# Revit family: 756-102-IS5-DN700-800
name_source: partatom
category: Pipe Accessories
units: mm (PartAtom-declared; Revit-internal decimal feet)

## family parameters
Always vertical = Yes
Cut with Voids When Loaded = No
Part Type = Valve - Breaks Into
Round Connector Dimension = Use Diameter
Shared = No
Work Plane-Based = No

## types (4) — shared parameters
A = 313 mm
A2 = 184 mm
Body_wallthickness = 10 mm  [stored 0.0328084 ft]
C_Rod = 38 mm  [stored 0.124672 ft]
D1 = 10 mm  [stored 0.0328084 ft]
DN0700_PN10 = 756-0700-1-04102
DN0700_PN16 = 756-0700-1-14102
DN0800_PN10 = 756-0800-1-04102
DN0800_PN16 = 756-0800-1-14102
Description_ = AVK DOUBLE ECC. BUTTERFLY VALVE, LONG
Disc_width = 40 mm  [stored 0.131234 ft]
Flange_Thickness = 40 mm  [stored 0.131234 ft]
GB_Flange = 5 mm  [stored 0.0164042 ft]
Gear_box_depth = 278 mm
Offset = 3 mm  [stored 0.00984252 ft]
Pin_dia = 60 mm  [stored 0.19685 ft]
RF_Cut_Thickness = 5 mm  [stored 0.0164042 ft]
Rib_depth = 30 mm  [stored 0.0984252 ft]
Search_table = 756-102-IS5-DN700-800
URL_product_pages = https://www.avkvalves.com

## per-type parameters (varying)
- DN0700_PN10: B=605 mm; Bottom_Depth=1050 mm; Bottom_width=395 mm; C=287 mm; DN=700 mm; Disc_Dia=690 mm; Flange_OD=448 mm; GB_Dia=40 mm  [stored 0.131234 ft]; GB_HW=125 mm  [stored 0.410105 ft]; GB_HW_2=42 mm; GB_Ref=17 mm; GB_Width=72 mm  [stored 0.23622 ft]; GB_Width_2=117 mm  [stored 0.383858 ft]; GB_Width_3=130 mm  [stored 0.426509 ft]; GB_Width_Ref=100 mm  [stored 0.328084 ft]; Gear_box_Mount_Flange_width=102 mm; Gear_box_Mount_width=16 mm; H1=565 mm; H2=550 mm; ID (Radius)=350 mm; L=430 mm; L1=127 mm; L2=133 mm  [stored 0.436352 ft]; Pin_Depth=798 mm; Pin_width=215 mm; Rf_Dia=397 mm; Rib_height=407 mm; Rib_height_2=118 mm; Rib_width=350 mm; Rib_width_2=204 mm  [stored 0.669291 ft]; T(Addon)=605 mm; W1=448 mm; W2=656 mm; W2_Ref=125 mm  [stored 0.410105 ft]; W3=533 mm; W4=543 mm
- DN0700_PN16: B=600 mm; Bottom_Depth=1050 mm; Bottom_width=427 mm; C=329 mm; DN=700 mm; Disc_Dia=690 mm; Flange_OD=455 mm; GB_Dia=40 mm  [stored 0.131234 ft]; GB_HW=125 mm  [stored 0.410105 ft]; GB_HW_2=42 mm; GB_Ref=17 mm; GB_Width=114 mm  [stored 0.374016 ft]; GB_Width_2=117 mm  [stored 0.383858 ft]; GB_Width_3=130 mm  [stored 0.426509 ft]; GB_Width_Ref=143 mm  [stored 0.46916 ft]; Gear_box_Mount_Flange_width=107 mm  [stored 0.35105 ft]; Gear_box_Mount_width=17 mm; H1=560 mm; H2=550 mm; ID (Radius)=350 mm; L=430 mm; L1=127 mm; L2=133 mm  [stored 0.436352 ft]; Pin_Depth=805 mm; Pin_width=215 mm; Rf_Dia=397 mm; Rib_height=414 mm; Rib_height_2=105 mm  [stored 0.344488 ft]; Rib_width=350 mm; Rib_width_2=214 mm  [stored 0.7021 ft]; T(Addon)=600 mm; W1=455 mm; W2=656 mm; W2_Ref=110 mm  [stored 0.360892 ft]; W3=533 mm; W4=543 mm
- DN0800_PN10: B=670 mm; Bottom_Depth=1200 mm; Bottom_width=460 mm; C=349 mm; DN=800 mm; Disc_Dia=789 mm; Flange_OD=508 mm; GB_Dia=41 mm; GB_HW=155 mm  [stored 0.50853 ft]; GB_HW_2=52 mm; GB_Ref=21 mm; GB_Width=114 mm  [stored 0.374016 ft]; GB_Width_2=126 mm  [stored 0.413386 ft]; GB_Width_3=140 mm  [stored 0.459318 ft]; GB_Width_Ref=157 mm  [stored 0.515092 ft]; Gear_box_Mount_Flange_width=112 mm; Gear_box_Mount_width=17 mm; H1=630 mm; H2=620 mm; ID (Radius)=400 mm; L=470 mm; L1=156 mm  [stored 0.511811 ft]; L2=162 mm  [stored 0.531496 ft]; Pin_Depth=908 mm; Pin_width=235 mm; Rf_Dia=450 mm; Rib_height=461 mm; Rib_height_2=123 mm; Rib_width=390 mm; Rib_width_2=223 mm; T(Addon)=670 mm; W1=508 mm; W2=735 mm; W2_Ref=155 mm  [stored 0.50853 ft]; W3=627 mm; W4=636 mm
- DN0800_PN16: B=670 mm; Bottom_Depth=1200 mm; Bottom_width=492 mm; C=349 mm; DN=800 mm; Disc_Dia=789 mm; Flange_OD=513 mm; GB_Dia=41 mm; GB_HW=155 mm  [stored 0.50853 ft]; GB_HW_2=52 mm; GB_Ref=21 mm; GB_Width=114 mm  [stored 0.374016 ft]; GB_Width_2=126 mm  [stored 0.413386 ft]; GB_Width_3=140 mm  [stored 0.459318 ft]; GB_Width_Ref=157 mm  [stored 0.515092 ft]; Gear_box_Mount_Flange_width=116 mm  [stored 0.380577 ft]; Gear_box_Mount_width=18 mm  [stored 0.0590551 ft]; H1=630 mm; H2=620 mm; ID (Radius)=400 mm; L=470 mm; L1=156 mm  [stored 0.511811 ft]; L2=162 mm  [stored 0.531496 ft]; Pin_Depth=913 mm; Pin_width=235 mm; Rf_Dia=450 mm; Rib_height=466 mm; Rib_height_2=118 mm; Rib_width=390 mm; Rib_width_2=232 mm; T(Addon)=670 mm; W1=513 mm; W2=735 mm; W2_Ref=155 mm  [stored 0.50853 ft]; W3=627 mm; W4=636 mm

note: [stored X ft] marks values corroborated as IEEE doubles in the binary element streams (Revit-internal decimal feet)

## geometry (parser evidence)
native form markers: Sweep x4
no freeform markers — native parametric forms only
